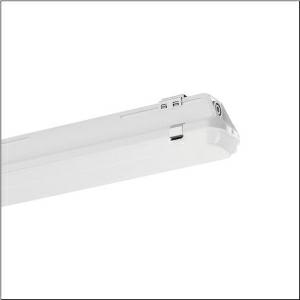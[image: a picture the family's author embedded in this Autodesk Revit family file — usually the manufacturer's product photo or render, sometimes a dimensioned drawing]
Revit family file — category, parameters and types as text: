
# Revit family: monsun_r__21_51fb107l420k_fe49
name_source: partatom
category: Lighting Fixtures
units: mm (PartAtom-declared; Revit-internal decimal feet)

## family parameters
Cut with Voids When Loaded = No
Host = Face
Light Source = No
Part Type = Normal
Room Calculation Point = No
Round Connector Dimension = Use Diameter
Shared = No

## types (1)
- Monsun® 21 (1 x LED, 2590 lm, 15.6 W, 4000K)
    Apparent Load = 16 VA
    CIE Flux Codes = 46 76 93 94 100
    Color Rendering = 80
    Color Temperature = 4000K
    Default Elevation = 1800 mm
    Description = Monsun® 21, damp-proof luminaire, chain hanger, primary optical cover: enclosure, of PMMA, light emission: direct distribution, primary light characteristic: symmetric, installation type: vertical mounting, horizontal mounting, surface-mounted, suspended mounting, LED, rated luminous flux: 2.590lm, luminous efficacy: 166lm/W, light colour: 840, colour temperature: 4000K, control gear: ON/OFF, with terminal, 3-pole, max. 2.5mm², mains connection: 220..240V, AC, 50/60Hz, rated input power: 16W, housing, of glass-fibre reinforced plastic, uncoated, bright grey, incl. chain hanger, length: 1.299mm, width: 90mm, height: 88mm, clip for enclosure, of stainless steel (V2A), ceiling mounting element, of stainless steel (V2A), chain hanger, of stainless steel (V2A), protection rating (complete): IP66, insulation class (complete): insulation class I (protective earthing), certification: CE, ENEC, VDE, UKCA, protection symbol: D, impact resistance: IK04, permissible operating ambient temperature: -25..+35°C, standard: EN 50419, EN 60598-2-1, corresponds to IFS (International Featured Standards) requirements for safety and quality in the food industry, for indoor or canopied outdoor use, no direct snow, no direct sun, no direct rain, LABS conformity tested according to VDMA 24364:2018-05, contact your sales advisor before using the luminaires in applications with unclear chemical exposure, large temperature fluctuations or condensation-forming humidity, packaging unit: 1 piece
    Height = 88 mm
    Lamp = 1 x LED
    Lamp Light Flux = 2590 lm
    Lamp Power = 15.6 W
    Lamp count = 1
    Length = 1299 mm
    Luminous efficacy = 166 lm/W
    Manufacturer = Siteco
    ModVariant = No
    Model = 51FB107L420K
    Mounting Place = Ceiling
    Mounting Type = Surface mounted
    Number of Poles = 1
    OnlyDefault = Yes
    Power Factor = 1
    Product Name = Monsun® 21
    Product group = damp-proof luminaire
    ProductGroupID = 300
    Protection Class = Protection class I
    Protection Degree = IP 66
    RLX_Detail_Level = 1
    RLX_Emergency_Light_Flux = 0 lm
    RLX_Emergency_Type = 0
    RLX_Emergency_Type_DB = No
    RlxData = <blob elided: 89569 chars, md5=fee077fb>
    Socket = socket
    Standby Power = 0 W
    System Light Flux = 2590 lm
    System Power = 16 W
    Type Comments = Product without accessories
    Type Image = l_1319656.jpg
    URL = http://relux.com
    VarID = ---
    Voltage = 0 V
    Weight = 0.00 kg
    Width = 90 mm

## geometry (parser evidence)
native form markers: Blend x4, Sweep x14
no freeform markers — native parametric forms only
